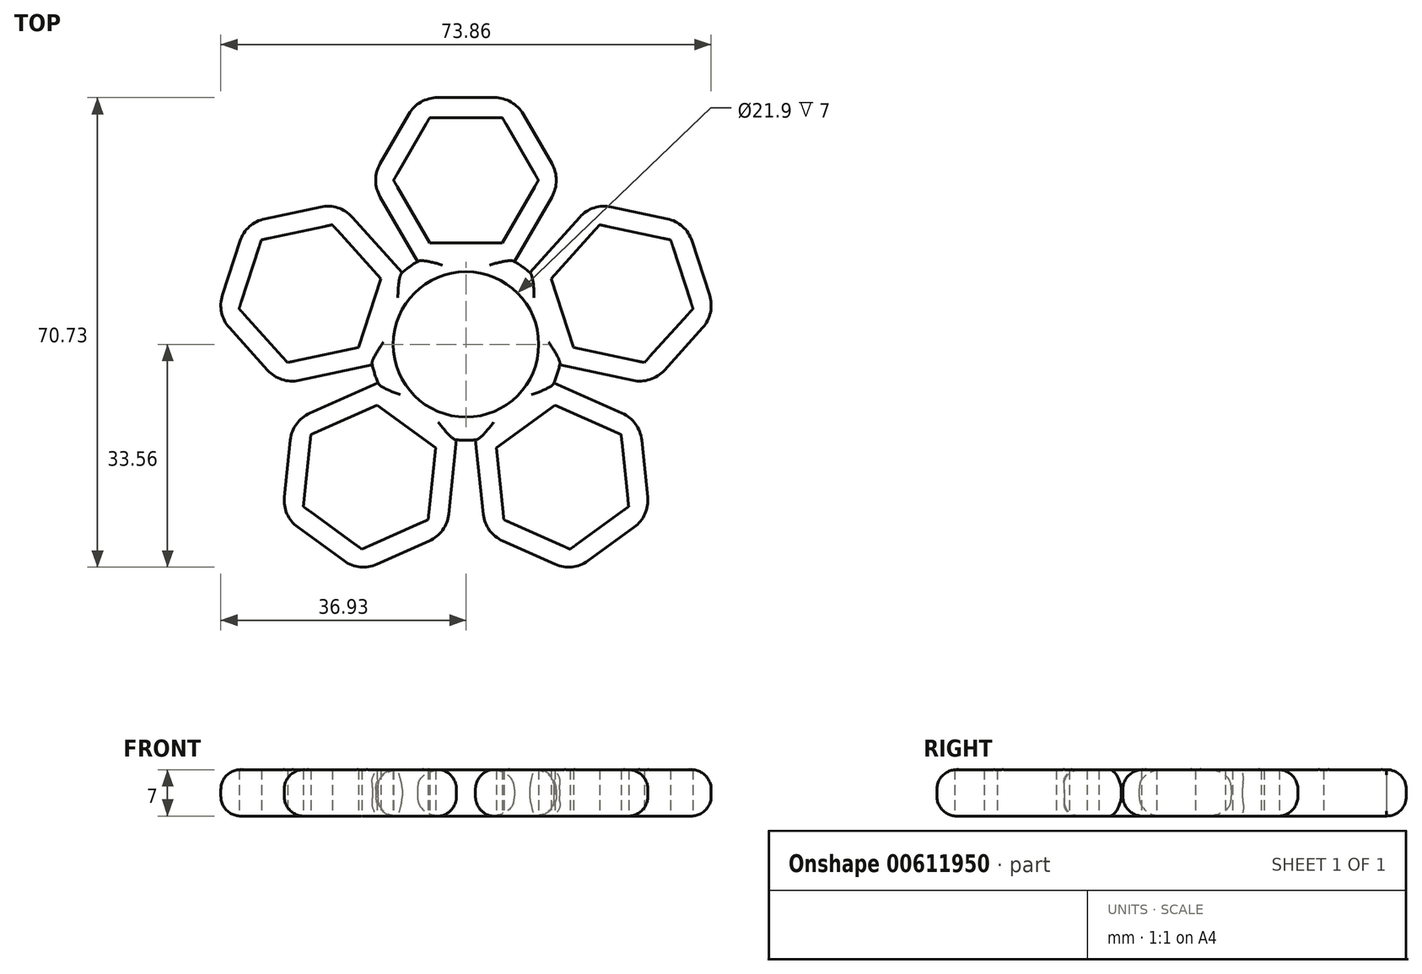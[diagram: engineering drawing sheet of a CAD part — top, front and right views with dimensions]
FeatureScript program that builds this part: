
annotation { "Feature Type Name" : "Feature", "Feature Type Description" : "" }
export const myFeature = defineFeature(function(context is Context, id is Id, definition is map)
    precondition{}
    {
        {
            var Q0;
            Q0=qCreatedBy(makeId("Top.planeOp"),FACE);
            var sketch = newSketch(context, id + "F0", { "sketchPlane" : qUnion([Q0])});
            skCircle(sketch, "E0", {"center": v(0, 0) * mm, "radius": 10.95 * mm});
            skCircle(sketch, "E1.0", {"center": v(0, 0) * mm, "radius": 14.45 * mm});
            skCircle(sketch, "E2.cCircle", {"center": v(0, 0) * mm, "radius": 20 * mm, "construction": true});
            skLineSegment(sketch, "E2.0", {"start": v(-23.51, 7.64) * mm, "end": v(0, 24.72) * mm, "construction": true});
            skLineSegment(sketch, "E2.1", {"start": v(0, 24.72) * mm, "end": v(23.51, 7.64) * mm, "construction": true});
            skLineSegment(sketch, "E2.2", {"start": v(23.51, 7.64) * mm, "end": v(14.53, -20) * mm, "construction": true});
            skLineSegment(sketch, "E2.3", {"start": v(14.53, -20) * mm, "end": v(-14.53, -20) * mm, "construction": true});
            skLineSegment(sketch, "E2.4", {"start": v(-14.53, -20) * mm, "end": v(-23.51, 7.64) * mm, "construction": true});
            skPoint(sketch, "E2.0.midPoint", {"position": v(-11.76, 16.18) * mm});
            skCircle(sketch, "E3.cCircle", {"center": v(0, 24.72) * mm, "radius": 9.45 * mm, "construction": true});
            skLineSegment(sketch, "E3.0", {"start": v(-5.46, 34.17) * mm, "end": v(5.46, 34.17) * mm});
            skLineSegment(sketch, "E3.1", {"start": v(5.46, 34.17) * mm, "end": v(10.91, 24.72) * mm});
            skLineSegment(sketch, "E3.2", {"start": v(10.91, 24.72) * mm, "end": v(5.46, 15.27) * mm});
            skLineSegment(sketch, "E3.3", {"start": v(5.46, 15.27) * mm, "end": v(-5.46, 15.27) * mm});
            skLineSegment(sketch, "E3.4", {"start": v(-5.46, 15.27) * mm, "end": v(-10.91, 24.72) * mm});
            skLineSegment(sketch, "E3.5", {"start": v(-10.91, 24.72) * mm, "end": v(-5.46, 34.17) * mm});
            skPoint(sketch, "E3.0.midPoint", {"position": v(0, 34.17) * mm});
            skCircle(sketch, "E4.cCircle", {"center": v(-23.51, 7.64) * mm, "radius": 9.45 * mm, "construction": true});
            skLineSegment(sketch, "E4.0", {"start": v(-34.18, 5.37) * mm, "end": v(-30.81, 15.75) * mm});
            skLineSegment(sketch, "E4.1", {"start": v(-30.81, 15.75) * mm, "end": v(-20.14, 18.02) * mm});
            skLineSegment(sketch, "E4.2", {"start": v(-20.14, 18.02) * mm, "end": v(-12.84, 9.9) * mm});
            skLineSegment(sketch, "E4.3", {"start": v(-12.84, 9.9) * mm, "end": v(-16.2, -0.47) * mm});
            skLineSegment(sketch, "E4.4", {"start": v(-16.2, -0.47) * mm, "end": v(-26.88, -2.74) * mm});
            skLineSegment(sketch, "E4.5", {"start": v(-26.88, -2.74) * mm, "end": v(-34.18, 5.37) * mm});
            skPoint(sketch, "E4.0.midPoint", {"position": v(-32.5, 10.56) * mm});
            skCircle(sketch, "E5.cCircle", {"center": v(-14.53, -20) * mm, "radius": 9.45 * mm, "construction": true});
            skLineSegment(sketch, "E5.0", {"start": v(-15.67, -30.85) * mm, "end": v(-24.5, -24.44) * mm});
            skLineSegment(sketch, "E5.1", {"start": v(-24.5, -24.44) * mm, "end": v(-23.36, -13.59) * mm});
            skLineSegment(sketch, "E5.2", {"start": v(-23.36, -13.59) * mm, "end": v(-13.4, -9.15) * mm});
            skLineSegment(sketch, "E5.3", {"start": v(-13.4, -9.15) * mm, "end": v(-4.56, -15.56) * mm});
            skLineSegment(sketch, "E5.4", {"start": v(-4.56, -15.56) * mm, "end": v(-5.7, -26.41) * mm});
            skLineSegment(sketch, "E5.5", {"start": v(-5.7, -26.41) * mm, "end": v(-15.67, -30.85) * mm});
            skPoint(sketch, "E5.0.midPoint", {"position": v(-20.09, -27.65) * mm});
            skCircle(sketch, "E6.cCircle", {"center": v(14.53, -20) * mm, "radius": 9.45 * mm, "construction": true});
            skLineSegment(sketch, "E6.0", {"start": v(24.5, -24.44) * mm, "end": v(15.67, -30.85) * mm});
            skLineSegment(sketch, "E6.1", {"start": v(15.67, -30.85) * mm, "end": v(5.7, -26.41) * mm});
            skLineSegment(sketch, "E6.2", {"start": v(5.7, -26.41) * mm, "end": v(4.56, -15.56) * mm});
            skLineSegment(sketch, "E6.3", {"start": v(4.56, -15.56) * mm, "end": v(13.4, -9.15) * mm});
            skLineSegment(sketch, "E6.4", {"start": v(13.4, -9.15) * mm, "end": v(23.36, -13.59) * mm});
            skLineSegment(sketch, "E6.5", {"start": v(23.36, -13.59) * mm, "end": v(24.5, -24.44) * mm});
            skPoint(sketch, "E6.0.midPoint", {"position": v(20.09, -27.65) * mm});
            skCircle(sketch, "E7.cCircle", {"center": v(23.51, 7.64) * mm, "radius": 9.45 * mm, "construction": true});
            skLineSegment(sketch, "E7.0", {"start": v(30.81, 15.75) * mm, "end": v(34.18, 5.37) * mm});
            skLineSegment(sketch, "E7.1", {"start": v(34.18, 5.37) * mm, "end": v(26.88, -2.74) * mm});
            skLineSegment(sketch, "E7.2", {"start": v(26.88, -2.74) * mm, "end": v(16.2, -0.47) * mm});
            skLineSegment(sketch, "E7.3", {"start": v(16.2, -0.47) * mm, "end": v(12.84, 9.9) * mm});
            skLineSegment(sketch, "E7.4", {"start": v(12.84, 9.9) * mm, "end": v(20.14, 18.02) * mm});
            skLineSegment(sketch, "E7.5", {"start": v(20.14, 18.02) * mm, "end": v(30.81, 15.75) * mm});
            skPoint(sketch, "E7.0.midPoint", {"position": v(32.5, 10.56) * mm});
            skLineSegment(sketch, "E8.0", {"start": v(9.45, 10.63) * mm, "end": v(19.07, 21.31) * mm});
            skLineSegment(sketch, "E8.1", {"start": v(33.13, 18.32) * mm, "end": v(37.57, 4.65) * mm});
            skLineSegment(sketch, "E8.2", {"start": v(37.57, 4.65) * mm, "end": v(27.95, -6.03) * mm});
            skLineSegment(sketch, "E8.3", {"start": v(19.07, 21.31) * mm, "end": v(33.13, 18.32) * mm});
            skLineSegment(sketch, "E8.4", {"start": v(27.95, -6.03) * mm, "end": v(13.9, -3.04) * mm});
            skLineSegment(sketch, "E8.5", {"start": v(13.9, -3.04) * mm, "end": v(9.45, 10.63) * mm});
            skLineSegment(sketch, "E9.0", {"start": v(-14.38, 24.72) * mm, "end": v(-7.19, 37.17) * mm});
            skLineSegment(sketch, "E9.1", {"start": v(7.19, 37.17) * mm, "end": v(14.38, 24.72) * mm});
            skLineSegment(sketch, "E9.2", {"start": v(14.38, 24.72) * mm, "end": v(7.19, 12.27) * mm});
            skLineSegment(sketch, "E9.3", {"start": v(-7.19, 37.17) * mm, "end": v(7.19, 37.17) * mm});
            skLineSegment(sketch, "E9.4", {"start": v(7.19, 12.27) * mm, "end": v(-7.19, 12.27) * mm});
            skLineSegment(sketch, "E9.5", {"start": v(-7.19, 12.27) * mm, "end": v(-14.38, 24.72) * mm});
            skLineSegment(sketch, "E10.0", {"start": v(-37.57, 4.65) * mm, "end": v(-33.13, 18.32) * mm});
            skLineSegment(sketch, "E10.1", {"start": v(-19.07, 21.31) * mm, "end": v(-9.45, 10.63) * mm});
            skLineSegment(sketch, "E10.2", {"start": v(-9.45, 10.63) * mm, "end": v(-13.9, -3.04) * mm});
            skLineSegment(sketch, "E10.3", {"start": v(-33.13, 18.32) * mm, "end": v(-19.07, 21.31) * mm});
            skLineSegment(sketch, "E10.4", {"start": v(-13.9, -3.04) * mm, "end": v(-27.95, -6.03) * mm});
            skLineSegment(sketch, "E10.5", {"start": v(-27.95, -6.03) * mm, "end": v(-37.57, 4.65) * mm});
            skLineSegment(sketch, "E11.0", {"start": v(-27.66, -25.85) * mm, "end": v(-26.16, -11.55) * mm});
            skLineSegment(sketch, "E11.1", {"start": v(-13.03, -5.7) * mm, "end": v(-1.4, -14.15) * mm});
            skLineSegment(sketch, "E11.2", {"start": v(-1.4, -14.15) * mm, "end": v(-2.9, -28.45) * mm});
            skLineSegment(sketch, "E11.3", {"start": v(-26.16, -11.55) * mm, "end": v(-13.03, -5.7) * mm});
            skLineSegment(sketch, "E11.4", {"start": v(-2.9, -28.45) * mm, "end": v(-16.03, -34.3) * mm});
            skLineSegment(sketch, "E11.5", {"start": v(-16.03, -34.3) * mm, "end": v(-27.66, -25.85) * mm});
            skLineSegment(sketch, "E12.0", {"start": v(2.9, -28.45) * mm, "end": v(1.4, -14.15) * mm});
            skLineSegment(sketch, "E12.1", {"start": v(13.03, -5.7) * mm, "end": v(26.16, -11.55) * mm});
            skLineSegment(sketch, "E12.2", {"start": v(26.16, -11.55) * mm, "end": v(27.66, -25.85) * mm});
            skLineSegment(sketch, "E12.3", {"start": v(1.4, -14.15) * mm, "end": v(13.03, -5.7) * mm});
            skLineSegment(sketch, "E12.4", {"start": v(27.66, -25.85) * mm, "end": v(16.03, -34.3) * mm});
            skLineSegment(sketch, "E12.5", {"start": v(16.03, -34.3) * mm, "end": v(2.9, -28.45) * mm});
            skSolve(sketch);
        }
        {
            var Q0;
            Q0 = qSketchRegion(id + "F0", true);
            extrude(context, id + "F1", {"entities" : qUnion([Q0]), "depth" : 7 * mm, "offsetDistance" : 25 * mm});
        }
        {
            var Q0;
            Q0=makeQuery(id+"F1.opExtrude","SWEPT_EDGE",EDGE,{"disambiguationData":[OSD([sQuery(id+"F0.wireOp",EDGE,"E12.0"),sQuery(id+"F0.wireOp",EDGE,"E12.5")])]});
            var Q1;
            Q1=makeQuery(id+"F1.opExtrude","SWEPT_EDGE",EDGE,{"disambiguationData":[OSD([sQuery(id+"F0.wireOp",EDGE,"E12.2"),sQuery(id+"F0.wireOp",EDGE,"E12.4")])]});
            var Q2;
            Q2=makeQuery(id+"F1.opExtrude","SWEPT_EDGE",EDGE,{"disambiguationData":[OSD([sQuery(id+"F0.wireOp",EDGE,"E12.1"),sQuery(id+"F0.wireOp",EDGE,"E12.2")])]});
            var Q3;
            Q3=makeQuery(id+"F1.opExtrude","SWEPT_EDGE",EDGE,{"disambiguationData":[OSD([sQuery(id+"F0.wireOp",EDGE,"E8.2"),sQuery(id+"F0.wireOp",EDGE,"E8.4")])]});
            var Q4;
            Q4=makeQuery(id+"F1.opExtrude","SWEPT_EDGE",EDGE,{"disambiguationData":[OSD([sQuery(id+"F0.wireOp",EDGE,"E8.1"),sQuery(id+"F0.wireOp",EDGE,"E8.2")])]});
            var Q5;
            Q5=makeQuery(id+"F1.opExtrude","SWEPT_EDGE",EDGE,{"disambiguationData":[OSD([sQuery(id+"F0.wireOp",EDGE,"E8.1"),sQuery(id+"F0.wireOp",EDGE,"E8.3")])]});
            var Q6;
            Q6=makeQuery(id+"F1.opExtrude","SWEPT_EDGE",EDGE,{"disambiguationData":[OSD([sQuery(id+"F0.wireOp",EDGE,"E8.0"),sQuery(id+"F0.wireOp",EDGE,"E8.3")])]});
            var Q7;
            Q7=makeQuery(id+"F1.opExtrude","SWEPT_EDGE",EDGE,{"disambiguationData":[OSD([sQuery(id+"F0.wireOp",EDGE,"E9.1"),sQuery(id+"F0.wireOp",EDGE,"E9.2")])]});
            var Q8;
            Q8=makeQuery(id+"F1.opExtrude","SWEPT_EDGE",EDGE,{"disambiguationData":[OSD([sQuery(id+"F0.wireOp",EDGE,"E9.1"),sQuery(id+"F0.wireOp",EDGE,"E9.3")])]});
            var Q9;
            Q9=makeQuery(id+"F1.opExtrude","SWEPT_EDGE",EDGE,{"disambiguationData":[OSD([sQuery(id+"F0.wireOp",EDGE,"E9.0"),sQuery(id+"F0.wireOp",EDGE,"E9.3")])]});
            var Q10;
            Q10=makeQuery(id+"F1.opExtrude","SWEPT_EDGE",EDGE,{"disambiguationData":[OSD([sQuery(id+"F0.wireOp",EDGE,"E9.0"),sQuery(id+"F0.wireOp",EDGE,"E9.5")])]});
            var Q11;
            Q11=makeQuery(id+"F1.opExtrude","SWEPT_EDGE",EDGE,{"disambiguationData":[OSD([sQuery(id+"F0.wireOp",EDGE,"E10.1"),sQuery(id+"F0.wireOp",EDGE,"E10.3")])]});
            var Q12;
            Q12=makeQuery(id+"F1.opExtrude","SWEPT_EDGE",EDGE,{"disambiguationData":[OSD([sQuery(id+"F0.wireOp",EDGE,"E10.0"),sQuery(id+"F0.wireOp",EDGE,"E10.3")])]});
            var Q13;
            Q13=makeQuery(id+"F1.opExtrude","SWEPT_EDGE",EDGE,{"disambiguationData":[OSD([sQuery(id+"F0.wireOp",EDGE,"E10.0"),sQuery(id+"F0.wireOp",EDGE,"E10.5")])]});
            var Q14;
            Q14=makeQuery(id+"F1.opExtrude","SWEPT_EDGE",EDGE,{"disambiguationData":[OSD([sQuery(id+"F0.wireOp",EDGE,"E10.4"),sQuery(id+"F0.wireOp",EDGE,"E10.5")])]});
            var Q15;
            Q15=makeQuery(id+"F1.opExtrude","SWEPT_EDGE",EDGE,{"disambiguationData":[OSD([sQuery(id+"F0.wireOp",EDGE,"E11.0"),sQuery(id+"F0.wireOp",EDGE,"E11.3")])]});
            var Q16;
            Q16=makeQuery(id+"F1.opExtrude","SWEPT_EDGE",EDGE,{"disambiguationData":[OSD([sQuery(id+"F0.wireOp",EDGE,"E11.0"),sQuery(id+"F0.wireOp",EDGE,"E11.5")])]});
            var Q17;
            Q17=makeQuery(id+"F1.opExtrude","SWEPT_EDGE",EDGE,{"disambiguationData":[OSD([sQuery(id+"F0.wireOp",EDGE,"E11.4"),sQuery(id+"F0.wireOp",EDGE,"E11.5")])]});
            var Q18;
            Q18=makeQuery(id+"F1.opExtrude","SWEPT_EDGE",EDGE,{"disambiguationData":[OSD([sQuery(id+"F0.wireOp",EDGE,"E11.2"),sQuery(id+"F0.wireOp",EDGE,"E11.4")])]});
            var Q19;
            Q19=makeQuery(id+"F1.opExtrude","SWEPT_EDGE",EDGE,{"disambiguationData":[OSD([sQuery(id+"F0.wireOp",EDGE,"E12.4"),sQuery(id+"F0.wireOp",EDGE,"E12.5")])]});
            fillet(context, id + "F2", {"entities" : qUnion([Q0, Q1, Q2, Q3, Q4, Q5, Q6, Q7, Q8, Q9, Q10, Q11, Q12, Q13, Q14, Q15, Q16, Q17, Q18, Q19]), "radius" : 5 * mm, "tangentPropagation" : true, "allowEdgeOverflow" : false});
        }
        {
            var Q0;
            Q0=makeQuery(id+"F1.opExtrude","CAP_EDGE",EDGE,{"disambiguationData":[OSD([sQuery(id+"F0.wireOp",EDGE,"E11.4")])],"isStart":true});
            var Q1;
            Q1=makeQuery(id+"F1.opExtrude","CAP_EDGE",EDGE,{"disambiguationData":[OSD([sQuery(id+"F0.wireOp",EDGE,"E12.5")])],"isStart":true});
            var Q2;
            Q2=makeQuery(id+"F1.opExtrude","CAP_EDGE",EDGE,{"disambiguationData":[OSD([sQuery(id+"F0.wireOp",EDGE,"E8.2")])],"isStart":true});
            var Q3;
            Q3=makeQuery(id+"F1.opExtrude","CAP_EDGE",EDGE,{"disambiguationData":[OSD([sQuery(id+"F0.wireOp",EDGE,"E9.2")])],"isStart":true});
            var Q4;
            Q4=makeQuery(id+"F1.opExtrude","CAP_EDGE",EDGE,{"disambiguationData":[OSD([sQuery(id+"F0.wireOp",EDGE,"E10.3")])],"isStart":true});
            var Q5;
            Q5=makeQuery(id+"F1.opExtrude","CAP_EDGE",EDGE,{"disambiguationData":[OSD([sQuery(id+"F0.wireOp",EDGE,"E8.1")])],"isStart":false});
            var Q6;
            Q6=makeQuery(id+"F1.opExtrude","CAP_EDGE",EDGE,{"disambiguationData":[OSD([sQuery(id+"F0.wireOp",EDGE,"E12.2")])],"isStart":false});
            var Q7;
            Q7=makeQuery(id+"F1.opExtrude","CAP_EDGE",EDGE,{"disambiguationData":[OSD([sQuery(id+"F0.wireOp",EDGE,"E11.5")])],"isStart":false});
            var Q8;
            Q8=makeQuery(id+"F1.opExtrude","CAP_EDGE",EDGE,{"disambiguationData":[OSD([sQuery(id+"F0.wireOp",EDGE,"E10.5")])],"isStart":false});
            var Q9;
            Q9=makeQuery(id+"F1.opExtrude","CAP_EDGE",EDGE,{"disambiguationData":[OSD([sQuery(id+"F0.wireOp",EDGE,"E9.0")])],"isStart":false});
            fillet(context, id + "F3", {"entities" : qUnion([Q0, Q1, Q2, Q3, Q4, Q5, Q6, Q7, Q8, Q9]), "radius" : 3 * mm, "tangentPropagation" : true, "allowEdgeOverflow" : false});
        }
        {
            var Q0;
            {var subQ0=sQuery(id+"F0.wireOp",EDGE,"E1.0");Q0=makeQuery(id+"F1.opExtrude","CAP_EDGE",EDGE,{"disambiguationData":[OSD([subQ0]),TDD([makeQuery(id+"F0.imprint","IMPRINT",EDGE,{"disambiguationData":[TD([[makeQuery(id+"F0.imprint","INTERSECT",VERTEX,{"derivedFrom":[subQ0,sQuery(id+"F0.wireOp",EDGE,"E11.2")]}),-1.0]])],"derivedFrom":subQ0})])],"isStart":false});}
            var Q1;
            {var subQ0=sQuery(id+"F0.wireOp",EDGE,"E1.0");Q1=makeQuery(id+"F1.opExtrude","CAP_EDGE",EDGE,{"disambiguationData":[OSD([subQ0]),TDD([makeQuery(id+"F0.imprint","IMPRINT",EDGE,{"disambiguationData":[TD([[makeQuery(id+"F0.imprint","INTERSECT",VERTEX,{"derivedFrom":[subQ0,sQuery(id+"F0.wireOp",EDGE,"E12.1")]}),-1.0]])],"derivedFrom":subQ0})])],"isStart":false});}
            var Q2;
            {var subQ0=sQuery(id+"F0.wireOp",EDGE,"E1.0");Q2=makeQuery(id+"F1.opExtrude","CAP_EDGE",EDGE,{"disambiguationData":[OSD([subQ0]),TDD([makeQuery(id+"F0.imprint","IMPRINT",EDGE,{"disambiguationData":[TD([[makeQuery(id+"F0.imprint","INTERSECT",VERTEX,{"derivedFrom":[subQ0,sQuery(id+"F0.wireOp",EDGE,"E9.2")]}),1.0]])],"derivedFrom":subQ0})])],"isStart":false});}
            var Q3;
            {var subQ0=sQuery(id+"F0.wireOp",EDGE,"E1.0");Q3=makeQuery(id+"F1.opExtrude","CAP_EDGE",EDGE,{"disambiguationData":[OSD([subQ0]),TDD([makeQuery(id+"F0.imprint","IMPRINT",EDGE,{"disambiguationData":[TD([[makeQuery(id+"F0.imprint","INTERSECT",VERTEX,{"derivedFrom":[subQ0,sQuery(id+"F0.wireOp",EDGE,"E9.5")]}),-1.0]])],"derivedFrom":subQ0})])],"isStart":false});}
            var Q4;
            {var subQ0=sQuery(id+"F0.wireOp",EDGE,"E1.0");Q4=makeQuery(id+"F1.opExtrude","CAP_EDGE",EDGE,{"disambiguationData":[OSD([subQ0]),TDD([makeQuery(id+"F0.imprint","IMPRINT",EDGE,{"disambiguationData":[TD([[makeQuery(id+"F0.imprint","INTERSECT",VERTEX,{"derivedFrom":[subQ0,sQuery(id+"F0.wireOp",EDGE,"E10.4")]}),-1.0]])],"derivedFrom":subQ0})])],"isStart":false});}
            var Q5;
            {var subQ0=sQuery(id+"F0.wireOp",EDGE,"E1.0");Q5=makeQuery(id+"F1.opExtrude","CAP_EDGE",EDGE,{"disambiguationData":[OSD([subQ0]),TDD([makeQuery(id+"F0.imprint","IMPRINT",EDGE,{"disambiguationData":[TD([[makeQuery(id+"F0.imprint","INTERSECT",VERTEX,{"derivedFrom":[subQ0,sQuery(id+"F0.wireOp",EDGE,"E11.2")]}),-1.0]])],"derivedFrom":subQ0})])],"isStart":true});}
            var Q6;
            {var subQ0=sQuery(id+"F0.wireOp",EDGE,"E1.0");Q6=makeQuery(id+"F1.opExtrude","CAP_EDGE",EDGE,{"disambiguationData":[OSD([subQ0]),TDD([makeQuery(id+"F0.imprint","IMPRINT",EDGE,{"disambiguationData":[TD([[makeQuery(id+"F0.imprint","INTERSECT",VERTEX,{"derivedFrom":[subQ0,sQuery(id+"F0.wireOp",EDGE,"E12.1")]}),-1.0]])],"derivedFrom":subQ0})])],"isStart":true});}
            var Q7;
            {var subQ0=sQuery(id+"F0.wireOp",EDGE,"E1.0");Q7=makeQuery(id+"F1.opExtrude","CAP_EDGE",EDGE,{"disambiguationData":[OSD([subQ0]),TDD([makeQuery(id+"F0.imprint","IMPRINT",EDGE,{"disambiguationData":[TD([[makeQuery(id+"F0.imprint","INTERSECT",VERTEX,{"derivedFrom":[subQ0,sQuery(id+"F0.wireOp",EDGE,"E9.2")]}),1.0]])],"derivedFrom":subQ0})])],"isStart":true});}
            var Q8;
            {var subQ0=sQuery(id+"F0.wireOp",EDGE,"E1.0");Q8=makeQuery(id+"F1.opExtrude","CAP_EDGE",EDGE,{"disambiguationData":[OSD([subQ0]),TDD([makeQuery(id+"F0.imprint","IMPRINT",EDGE,{"disambiguationData":[TD([[makeQuery(id+"F0.imprint","INTERSECT",VERTEX,{"derivedFrom":[subQ0,sQuery(id+"F0.wireOp",EDGE,"E9.5")]}),-1.0]])],"derivedFrom":subQ0})])],"isStart":true});}
            var Q9;
            {var subQ0=sQuery(id+"F0.wireOp",EDGE,"E1.0");Q9=makeQuery(id+"F1.opExtrude","CAP_EDGE",EDGE,{"disambiguationData":[OSD([subQ0]),TDD([makeQuery(id+"F0.imprint","IMPRINT",EDGE,{"disambiguationData":[TD([[makeQuery(id+"F0.imprint","INTERSECT",VERTEX,{"derivedFrom":[subQ0,sQuery(id+"F0.wireOp",EDGE,"E10.4")]}),-1.0]])],"derivedFrom":subQ0})])],"isStart":true});}
            fillet(context, id + "F4", {"entities" : qUnion([Q0, Q1, Q2, Q3, Q4, Q5, Q6, Q7, Q8, Q9]), "radius" : 2 * mm, "tangentPropagation" : true, "allowEdgeOverflow" : false});
        }
    });
